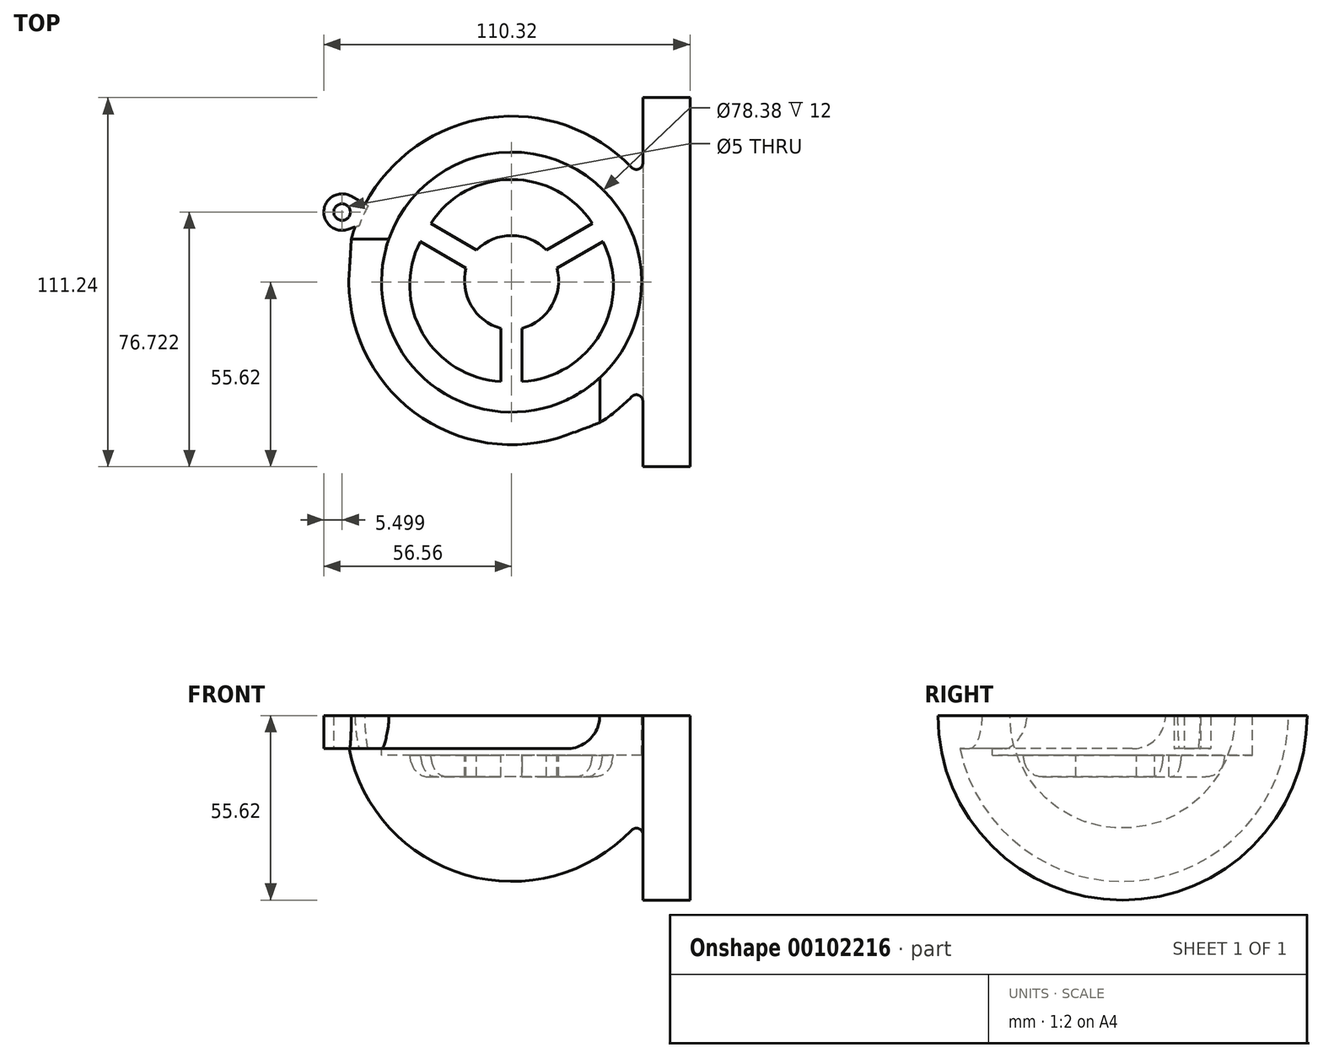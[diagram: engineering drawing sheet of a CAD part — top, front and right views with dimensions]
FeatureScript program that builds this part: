
annotation { "Feature Type Name" : "Feature", "Feature Type Description" : "" }
export const myFeature = defineFeature(function(context is Context, id is Id, definition is map)
    precondition{}
    {
        {
            var Q0;
            Q0=qCreatedBy(makeId("Top.planeOp"),FACE);
            var sketch = newSketch(context, id + "F0", { "sketchPlane" : qUnion([Q0])});
            skCircle(sketch, "E0", {"center": v(0, 0) * mm, "radius": 10 * mm});
            skSolve(sketch);
        }
        {
            var Q0;
            Q0=qCreatedBy(makeId("Front.planeOp"),FACE);
            var sketch = newSketch(context, id + "F1", { "sketchPlane" : qUnion([Q0])});
            skArc(sketch, "E1", {"start": v(-50, 0) * mm, "mid": v(0, -50) * mm, "end": v(50, 0) * mm});
            skLineSegment(sketch, "E2", {"start": v(-50, 0) * mm, "end": v(50, 0) * mm});
            skSolve(sketch);
        }
        {
            var Q0;
            Q0=makeQuery(id+"F1.imprint","IMPRINT",FACE,{"disambiguationData":[TD([[makeQuery(id+"F1.imprint","IMPRINT",EDGE,{"derivedFrom":sQuery(id+"F1.wireOp",EDGE,"E1")}),1.0]])]});
            var Q1;
            Q1=sQuery(id+"F1.wireOp",EDGE,"E2");
            revolve(context, id + "F2", {"entities" : qUnion([Q0]), "axis" : qUnion([Q1]), "revolveType" : RevolveType.SYMMETRIC, "angle" : 180 * degree});
        }
        {
            var Q0;
            Q0=makeQuery(id+"F0.imprint","IMPRINT",FACE,{"disambiguationData":[TD([[makeQuery(id+"F0.imprint","IMPRINT",EDGE,{"derivedFrom":sQuery(id+"F0.wireOp",EDGE,"E0")}),1.0]])]});
            var sketch = newSketch(context, id + "F3", { "sketchPlane" : qUnion([Q0])});
            skCircle(sketch, "E3", {"center": v(0, 0) * mm, "radius": 39.19 * mm});
            skSolve(sketch);
        }
        {
            var Q0;
            Q0 = qSketchRegion(id + "F3", true);
            var Q1;
            Q1=sQuery(id+"F3.wireOp",EDGE,"E3");
            extrude(context, id + "F4", {"entities" : qUnion([Q0]), "operationType" : NewBodyOperationType.REMOVE, "surfaceEntities" : qUnion([Q1]), "oppositeDirection" : true, "depth" : 12 * mm});
        }
        {
            var Q0;
            Q0=makeQuery(id+"F0.imprint","IMPRINT",FACE,{"disambiguationData":[TD([[makeQuery(id+"F0.imprint","IMPRINT",EDGE,{"derivedFrom":sQuery(id+"F0.wireOp",EDGE,"E0")}),1.0]])]});
            var sketch = newSketch(context, id + "F5", { "sketchPlane" : qUnion([Q0])});
            skLineSegment(sketch, "E4", {"start": v(-10.53, 9.73) * mm, "end": v(-20.87, 15.7) * mm});
            skLineSegment(sketch, "E5.MirrorCS", {"start": v(10.53, 9.73) * mm, "end": v(20.87, 15.7) * mm});
            skArc(sketch, "E6.trimOffspring", {"start": v(10.53, 9.73) * mm, "mid": v(0, 14.05) * mm, "end": v(-10.53, 9.73) * mm});
            skArc(sketch, "E7.trimOffspring", {"start": v(20.87, 15.7) * mm, "mid": v(0, 26.93) * mm, "end": v(-20.87, 15.7) * mm});
            skArc(sketch, "E8.1.0", {"start": v(-13.7, 4.26) * mm, "mid": v(-12.17, -7.02) * mm, "end": v(-3.16, -13.99) * mm});
            skLineSegment(sketch, "E8.1.1", {"start": v(-3.16, -13.99) * mm, "end": v(-3.16, -25.92) * mm});
            skArc(sketch, "E8.1.2", {"start": v(-24.03, 10.23) * mm, "mid": v(-23.32, -13.47) * mm, "end": v(-3.16, -25.92) * mm});
            skLineSegment(sketch, "E8.1.3", {"start": v(-13.7, 4.26) * mm, "end": v(-24.03, 10.23) * mm});
            skArc(sketch, "E8.2.0", {"start": v(3.16, -13.99) * mm, "mid": v(12.17, -7.02) * mm, "end": v(13.7, 4.26) * mm});
            skLineSegment(sketch, "E8.2.1", {"start": v(13.7, 4.26) * mm, "end": v(24.03, 10.23) * mm});
            skArc(sketch, "E8.2.2", {"start": v(3.16, -25.92) * mm, "mid": v(23.32, -13.47) * mm, "end": v(24.03, 10.23) * mm});
            skLineSegment(sketch, "E8.2.3", {"start": v(3.16, -13.99) * mm, "end": v(3.16, -25.92) * mm});
            skPoint(sketch, "E8.center", {"position": v(0, 0) * mm});
            skLineSegment(sketch, "E9", {"start": v(0, 52.56) * mm, "end": v(0, -56.48) * mm, "construction": true});
            skLineSegment(sketch, "E10", {"start": v(-55.73, 0) * mm, "end": v(59.64, 0) * mm, "construction": true});
            skSolve(sketch);
        }
        {
            var Q0;
            Q0=makeQuery(id+"F5.imprint","IMPRINT",FACE,{"disambiguationData":[TD([[makeQuery(id+"F5.imprint","IMPRINT",EDGE,{"derivedFrom":sQuery(id+"F5.wireOp",EDGE,"E4")}),-1.0]])]});
            var Q1;
            Q1=makeQuery(id+"F5.imprint","IMPRINT",FACE,{"disambiguationData":[TD([[makeQuery(id+"F5.imprint","IMPRINT",EDGE,{"derivedFrom":sQuery(id+"F5.wireOp",EDGE,"E8.1.0")}),-1.0]])]});
            var Q2;
            Q2=makeQuery(id+"F5.imprint","IMPRINT",FACE,{"disambiguationData":[TD([[makeQuery(id+"F5.imprint","IMPRINT",EDGE,{"derivedFrom":sQuery(id+"F5.wireOp",EDGE,"E8.2.0")}),-1.0]])]});
            extrude(context, id + "F6", {"entities" : qUnion([Q0, Q1, Q2]), "operationType" : NewBodyOperationType.REMOVE, "oppositeDirection" : true, "depth" : (12 + 6.5) * mm});
        }
        {
            var Q0;
            Q0=makeQuery(id+"F6.boolean.opBoolean","INTERSECT",EDGE,{"derivedFrom":[makeQuery(id+"F4.boolean.opBoolean","COPY",FACE,{"derivedFrom":makeQuery(id+"F4.opExtrude","CAP_FACE",FACE,{"disambiguationData":[OSD([sQuery(id+"F3.wireOp",EDGE,"E3")])],"isStart":false})}),makeQuery(id+"F6.opExtrude","SWEPT_FACE",FACE,{"disambiguationData":[OSD([sQuery(id+"F5.wireOp",EDGE,"E7.trimOffspring")])]})]});
            var Q1;
            Q1=makeQuery(id+"F6.boolean.opBoolean","INTERSECT",EDGE,{"derivedFrom":[makeQuery(id+"F4.boolean.opBoolean","COPY",FACE,{"derivedFrom":makeQuery(id+"F4.opExtrude","CAP_FACE",FACE,{"disambiguationData":[OSD([sQuery(id+"F3.wireOp",EDGE,"E3")])],"isStart":false})}),makeQuery(id+"F6.opExtrude","SWEPT_FACE",FACE,{"disambiguationData":[OSD([sQuery(id+"F5.wireOp",EDGE,"E8.1.2")])]})]});
            var Q2;
            Q2=makeQuery(id+"F6.boolean.opBoolean","INTERSECT",EDGE,{"derivedFrom":[makeQuery(id+"F4.boolean.opBoolean","COPY",FACE,{"derivedFrom":makeQuery(id+"F4.opExtrude","CAP_FACE",FACE,{"disambiguationData":[OSD([sQuery(id+"F3.wireOp",EDGE,"E3")])],"isStart":false})}),makeQuery(id+"F6.opExtrude","SWEPT_FACE",FACE,{"disambiguationData":[OSD([sQuery(id+"F5.wireOp",EDGE,"E8.2.2")])]})]});
            chamfer(context, id + "F7", {"entities" : qUnion([Q0, Q1, Q2]), "chamferType" : ChamferType.TWO_OFFSETS, "width1" : 19 * mm, "oppositeDirection" : false, "width2" : 4 * mm, "tangentPropagation" : true});
        }
        {
            var Q0;
            Q0=qCreatedBy(makeId("Front.planeOp"),FACE);
            var sketch = newSketch(context, id + "F8", { "sketchPlane" : qUnion([Q0])});
            skLineSegment(sketch, "E11.bottom", {"start": v(39.58, 0) * mm, "end": v(53.76, 0) * mm});
            skLineSegment(sketch, "E11.top", {"start": v(39.58, -55.62) * mm, "end": v(53.76, -55.62) * mm});
            skLineSegment(sketch, "E11.left", {"start": v(39.58, 0) * mm, "end": v(39.58, -55.62) * mm});
            skLineSegment(sketch, "E11.right", {"start": v(53.76, 0) * mm, "end": v(53.76, -55.62) * mm});
            skSolve(sketch);
        }
        {
            var Q0;
            Q0=makeQuery(id+"F8.imprint","IMPRINT",FACE,{"disambiguationData":[TD([[makeQuery(id+"F8.imprint","IMPRINT",EDGE,{"derivedFrom":sQuery(id+"F8.wireOp",EDGE,"E11.bottom")}),-1.0]])]});
            var Q1;
            Q1=sQuery(id+"F8.wireOp",EDGE,"E11.bottom");
            revolve(context, id + "F9", {"operationType" : NewBodyOperationType.ADD, "entities" : qUnion([Q0]), "axis" : qUnion([Q1]), "revolveType" : RevolveType.SYMMETRIC, "angle" : 180 * degree});
        }
        {
            var Q0;
            Q0=makeQuery(id+"F9.boolean.opBoolean","INTERSECT",EDGE,{"derivedFrom":[makeQuery(id+"F2.opRevolve","SWEPT_FACE",FACE,{"disambiguationData":[OSD([sQuery(id+"F1.wireOp",EDGE,"E1")])]}),makeQuery(id+"F9.opRevolve","SWEPT_FACE",FACE,{"disambiguationData":[OSD([sQuery(id+"F8.wireOp",EDGE,"E11.left")])]})]});
            fillet(context, id + "F10", {"entities" : qUnion([Q0]), "radius" : 2 * mm, "tangentPropagation" : true, "allowEdgeOverflow" : false});
        }
        {
            var Q0;
            Q0=makeQuery(id+"F9.boolean.opBoolean","MERGE",FACE,{"derivedFrom":[makeQuery(id+"F2.opRevolve","CAP_FACE",FACE,{"disambiguationData":[OSD([sQuery(id+"F1.wireOp",EDGE,"E1"),sQuery(id+"F1.wireOp",EDGE,"E2")])],"isStart":true}),makeQuery(id+"F9.opRevolve","CAP_FACE",FACE,{"disambiguationData":[OSD([sQuery(id+"F8.wireOp",EDGE,"E11.bottom"),sQuery(id+"F8.wireOp",EDGE,"E11.top"),sQuery(id+"F8.wireOp",EDGE,"E11.left"),sQuery(id+"F8.wireOp",EDGE,"E11.right")])],"isStart":true})]});
            var sketch = newSketch(context, id + "F11", { "sketchPlane" : qUnion([Q0])});
            skLineSegment(sketch, "E12", {"start": v(-48.28, 13) * mm, "end": v(-36.97, 13) * mm});
            skLineSegment(sketch, "E13", {"start": v(26.58, -28.8) * mm, "end": v(26.58, -42.35) * mm});
            skSolve(sketch);
        }
        {
            var Q0;
            {var subQ0=sQuery(id+"F11.wireOp",EDGE,"E12");Q0=makeQuery(id+"F11.imprint","IMPRINT",FACE,{"disambiguationData":[TD([[makeQuery(id+"F11.imprint","IMPRINT",EDGE,{"derivedFrom":subQ0}),-1.0]])]});}
            extrude(context, id + "F12", {"entities" : qUnion([Q0]), "operationType" : NewBodyOperationType.REMOVE, "oppositeDirection" : true, "depth" : 10 * mm});
        }
        {
            var Q0;
            Q0=makeQuery(id+"F12.boolean.opBoolean","COPY",EDGE,{"derivedFrom":makeQuery(id+"F12.opExtrude","CAP_EDGE",EDGE,{"disambiguationData":[OSD([sQuery(id+"F11.wireOp",EDGE,"E12")])],"isStart":false})});
            var Q1;
            Q1=makeQuery(id+"F12.boolean.opBoolean","COPY",EDGE,{"derivedFrom":makeQuery(id+"F12.opExtrude","CAP_EDGE",EDGE,{"disambiguationData":[OSD([sQuery(id+"F11.wireOp",EDGE,"E13")])],"isStart":false})});
            fillet(context, id + "F13", {"entities" : qUnion([Q0, Q1]), "radius" : 10 * mm, "tangentPropagation" : true, "allowEdgeOverflow" : false});
        }
        {
            var Q0;
            Q0=makeQuery(id+"F9.boolean.opBoolean","MERGE",FACE,{"derivedFrom":[makeQuery(id+"F2.opRevolve","CAP_FACE",FACE,{"disambiguationData":[OSD([sQuery(id+"F1.wireOp",EDGE,"E1"),sQuery(id+"F1.wireOp",EDGE,"E2")])],"isStart":true}),makeQuery(id+"F9.opRevolve","CAP_FACE",FACE,{"disambiguationData":[OSD([sQuery(id+"F8.wireOp",EDGE,"E11.bottom"),sQuery(id+"F8.wireOp",EDGE,"E11.top"),sQuery(id+"F8.wireOp",EDGE,"E11.left"),sQuery(id+"F8.wireOp",EDGE,"E11.right")])],"isStart":true})]});
            cPlane(context, id + "F14", {"entities" : qUnion([Q0]), "cplaneType" : CPlaneType.OFFSET, "offset" : 10 * mm, "oppositeDirection" : true, "width" : 150 * mm, "height" : 150 * mm});
        }
        {
            var Q0;
            Q0=qCreatedBy(id+"F14.planeOp",FACE);
            var sketch = newSketch(context, id + "F15", { "sketchPlane" : qUnion([Q0])});
            skCircle(sketch, "E14", {"center": v(-51.06, 21.1) * mm, "radius": 2.5 * mm});
            skArc(sketch, "E15", {"start": v(-48.32, 25.87) * mm, "mid": v(-56.53, 21.65) * mm, "end": v(-49.33, 15.88) * mm});
            skLineSegment(sketch, "E16", {"start": v(-48.32, 25.87) * mm, "end": v(-40.04, 21.1) * mm});
            skPoint(sketch, "E17", {"position": v(-45.62, 20.32) * mm});
            skLineSegment(sketch, "E18", {"start": v(-41.9, 18.35) * mm, "end": v(-40.04, 21.1) * mm});
            skLineSegment(sketch, "E19", {"start": v(-41.9, 18.35) * mm, "end": v(-49.33, 15.88) * mm});
            skSolve(sketch);
        }
        {
            var Q0;
            Q0=makeQuery(id+"F15.imprint","IMPRINT",FACE,{"disambiguationData":[TD([[makeQuery(id+"F15.imprint","IMPRINT",EDGE,{"derivedFrom":sQuery(id+"F15.wireOp",EDGE,"E14")}),-1.0]])]});
            extrude(context, id + "F16", {"entities" : qUnion([Q0]), "operationType" : NewBodyOperationType.ADD, "depth" : 10 * mm});
        }
        {
            var Q0;
            {var subQ0=sQuery(id+"F5.wireOp",EDGE,"E8.1.2");Q0=makeQuery(id+"F7.opChamfer","BLEND_EDGE",EDGE,{"blendedFrom":[makeQuery(id+"F6.boolean.opBoolean","INTERSECT",EDGE,{"derivedFrom":[makeQuery(id+"F4.boolean.opBoolean","COPY",FACE,{"derivedFrom":makeQuery(id+"F4.opExtrude","CAP_FACE",FACE,{"disambiguationData":[OSD([sQuery(id+"F3.wireOp",EDGE,"E3")])],"isStart":false})}),makeQuery(id+"F6.opExtrude","SWEPT_FACE",FACE,{"disambiguationData":[OSD([subQ0])]})]}),makeQuery(id+"F6.boolean.opBoolean","COPY",FACE,{"derivedFrom":makeQuery(id+"F6.opExtrude","CAP_FACE",FACE,{"disambiguationData":[OSD([sQuery(id+"F5.wireOp",EDGE,"E8.1.0"),sQuery(id+"F5.wireOp",EDGE,"E8.1.1"),subQ0,sQuery(id+"F5.wireOp",EDGE,"E8.1.3")])],"isStart":false})})],"blendedInto":[makeQuery(id+"F6.boolean.opBoolean","COPY",FACE,{"derivedFrom":makeQuery(id+"F6.opExtrude","CAP_FACE",FACE,{"disambiguationData":[OSD([sQuery(id+"F5.wireOp",EDGE,"E8.1.0"),sQuery(id+"F5.wireOp",EDGE,"E8.1.1"),subQ0,sQuery(id+"F5.wireOp",EDGE,"E8.1.3")])],"isStart":false})})]});}
            var Q1;
            {var subQ0=sQuery(id+"F5.wireOp",EDGE,"E7.trimOffspring");Q1=makeQuery(id+"F7.opChamfer","BLEND_EDGE",EDGE,{"blendedFrom":[makeQuery(id+"F6.boolean.opBoolean","INTERSECT",EDGE,{"derivedFrom":[makeQuery(id+"F4.boolean.opBoolean","COPY",FACE,{"derivedFrom":makeQuery(id+"F4.opExtrude","CAP_FACE",FACE,{"disambiguationData":[OSD([sQuery(id+"F3.wireOp",EDGE,"E3")])],"isStart":false})}),makeQuery(id+"F6.opExtrude","SWEPT_FACE",FACE,{"disambiguationData":[OSD([subQ0])]})]}),makeQuery(id+"F6.boolean.opBoolean","COPY",FACE,{"derivedFrom":makeQuery(id+"F6.opExtrude","CAP_FACE",FACE,{"disambiguationData":[OSD([sQuery(id+"F5.wireOp",EDGE,"E4"),sQuery(id+"F5.wireOp",EDGE,"E5.MirrorCS"),sQuery(id+"F5.wireOp",EDGE,"E6.trimOffspring"),subQ0])],"isStart":false})})],"blendedInto":[makeQuery(id+"F6.boolean.opBoolean","COPY",FACE,{"derivedFrom":makeQuery(id+"F6.opExtrude","CAP_FACE",FACE,{"disambiguationData":[OSD([sQuery(id+"F5.wireOp",EDGE,"E4"),sQuery(id+"F5.wireOp",EDGE,"E5.MirrorCS"),sQuery(id+"F5.wireOp",EDGE,"E6.trimOffspring"),subQ0])],"isStart":false})})]});}
            var Q2;
            {var subQ0=sQuery(id+"F5.wireOp",EDGE,"E8.2.2");Q2=makeQuery(id+"F7.opChamfer","BLEND_EDGE",EDGE,{"blendedFrom":[makeQuery(id+"F6.boolean.opBoolean","INTERSECT",EDGE,{"derivedFrom":[makeQuery(id+"F4.boolean.opBoolean","COPY",FACE,{"derivedFrom":makeQuery(id+"F4.opExtrude","CAP_FACE",FACE,{"disambiguationData":[OSD([sQuery(id+"F3.wireOp",EDGE,"E3")])],"isStart":false})}),makeQuery(id+"F6.opExtrude","SWEPT_FACE",FACE,{"disambiguationData":[OSD([subQ0])]})]}),makeQuery(id+"F6.boolean.opBoolean","COPY",FACE,{"derivedFrom":makeQuery(id+"F6.opExtrude","CAP_FACE",FACE,{"disambiguationData":[OSD([sQuery(id+"F5.wireOp",EDGE,"E8.2.0"),sQuery(id+"F5.wireOp",EDGE,"E8.2.1"),subQ0,sQuery(id+"F5.wireOp",EDGE,"E8.2.3")])],"isStart":false})})],"blendedInto":[makeQuery(id+"F6.boolean.opBoolean","COPY",FACE,{"derivedFrom":makeQuery(id+"F6.opExtrude","CAP_FACE",FACE,{"disambiguationData":[OSD([sQuery(id+"F5.wireOp",EDGE,"E8.2.0"),sQuery(id+"F5.wireOp",EDGE,"E8.2.1"),subQ0,sQuery(id+"F5.wireOp",EDGE,"E8.2.3")])],"isStart":false})})]});}
            fillet(context, id + "F17", {"entities" : qUnion([Q0, Q1, Q2]), "radius" : 5.5 * mm, "tangentPropagation" : true, "allowEdgeOverflow" : false});
        }
    });
